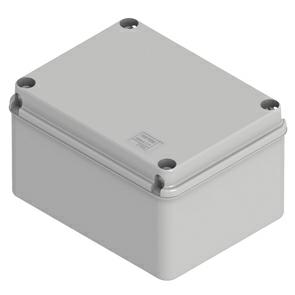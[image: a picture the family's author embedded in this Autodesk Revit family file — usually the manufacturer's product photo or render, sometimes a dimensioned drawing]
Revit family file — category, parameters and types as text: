
# Revit family: Building-SurfaceMountingEnclosures-GEWISS-44CE-JUNCTION-BOXES-WALL-MOUNTING_HIGH_CAPACITY
name_source: partatom
category: Apparecchi elettrici
revit_build: Autodesk Revit 2016 (Build: 20161004_0715(x64)
units: mm (PartAtom-declared; Revit-internal decimal feet)

## family parameters
Condiviso = No
Host = Superficie
Mantenere orientamento annotazione = Sì
Numero OmniClass = 23.80.30.14.24
Punto di calcolo locali = Sì
Quota connettore circolare = Usa diametro
Taglio con vuoti quando caricato = No
Tipo di parte = Normale
Titolo OmniClass = Junction Boxes

## types (1)
- Building-SurfaceMountingEnclosures-GEWISS-44CE-JUNCTION-BOXES-WALL-MOUNTING_HIGH_CAPACITY
    Accessories for insulation restoring = GW44621, GW44623
    Application = Ordinary junctions
    Carico apparente = 0 VA
    Catalogue = BUILDING
    Catalogue Range = 44 CE
    Classificazione = Other
    Colour = Grey RAL 7035
    Coperchio = GEWISS COPERCHIO TRASPARENTE
    Descrizione = JUNCT.BOX H.CAP.BOT.380X300X170 TRAN.COV
    Dettaglio = Elemento di dettaglio - 44CE alta capienza : 380x300x120
    EAN code = 8011564763562
    Effective height of bottom = 119 mm
    Electrocod = 02210
    GEWISS SCHEDA TECNICA = http://pro.gewiss.com
    Glow Wire Test = 650°C
    IDF = e1677b07-8b63-4b85-b946-96fa560cf2b7
    IDT = 54e6e708-f22e-4f1e-b852-9ec59277bb73
    IP degree = IP56
    Immagine tipo = GW44140.jpg
    Insulation class = II (according to IEC 61140 standards)
    Internal dim. LxHxD (mm) = 380x300x170
    Larghezza_interna = 380 mm
    Lid = Plain screwed
    Lid colour = Transparent
    Lid screws (no. and type) = 4 insul. sealable hinged
    Lunghezza_interna = 300 mm
    Material = Technopolymer GWPLAST 75
    Max Ã˜ holes possible = 54MM
    Modello = GW44140
    Operating temperature = -25 +60 °C
    Produttore = GEWISS S.p.A.
    Prospetto di default = 1219 mm
    SEO = Box
    Scatola = GEWISS SCATOLA
    Shock resistance = IK08
    Spessore = 170 mm  [stored 0.557743 ft]
    Technical sheet = https://www.gewiss.com
    Thermo-pressure with ball = 85
    Torque screws tightening = 1,8NM
    Type of bottom = High capacity
    Type of material = Halogen-free in compliance with EN 60754-2
    URL = https://www.gewiss.com
    Version file RFA = 18.0
    Voltaggio_x = 0 V
    Walls = Smooth

note: source unit labels omitted for Thermo-pressure with ball — the stored unit's dimension contradicts the parameter name (converter mislabeling)

note: [stored X ft] marks values corroborated as IEEE doubles in the binary element streams (Revit-internal decimal feet)

## geometry (parser evidence)
native form markers: Blend x4
no freeform markers — native parametric forms only
